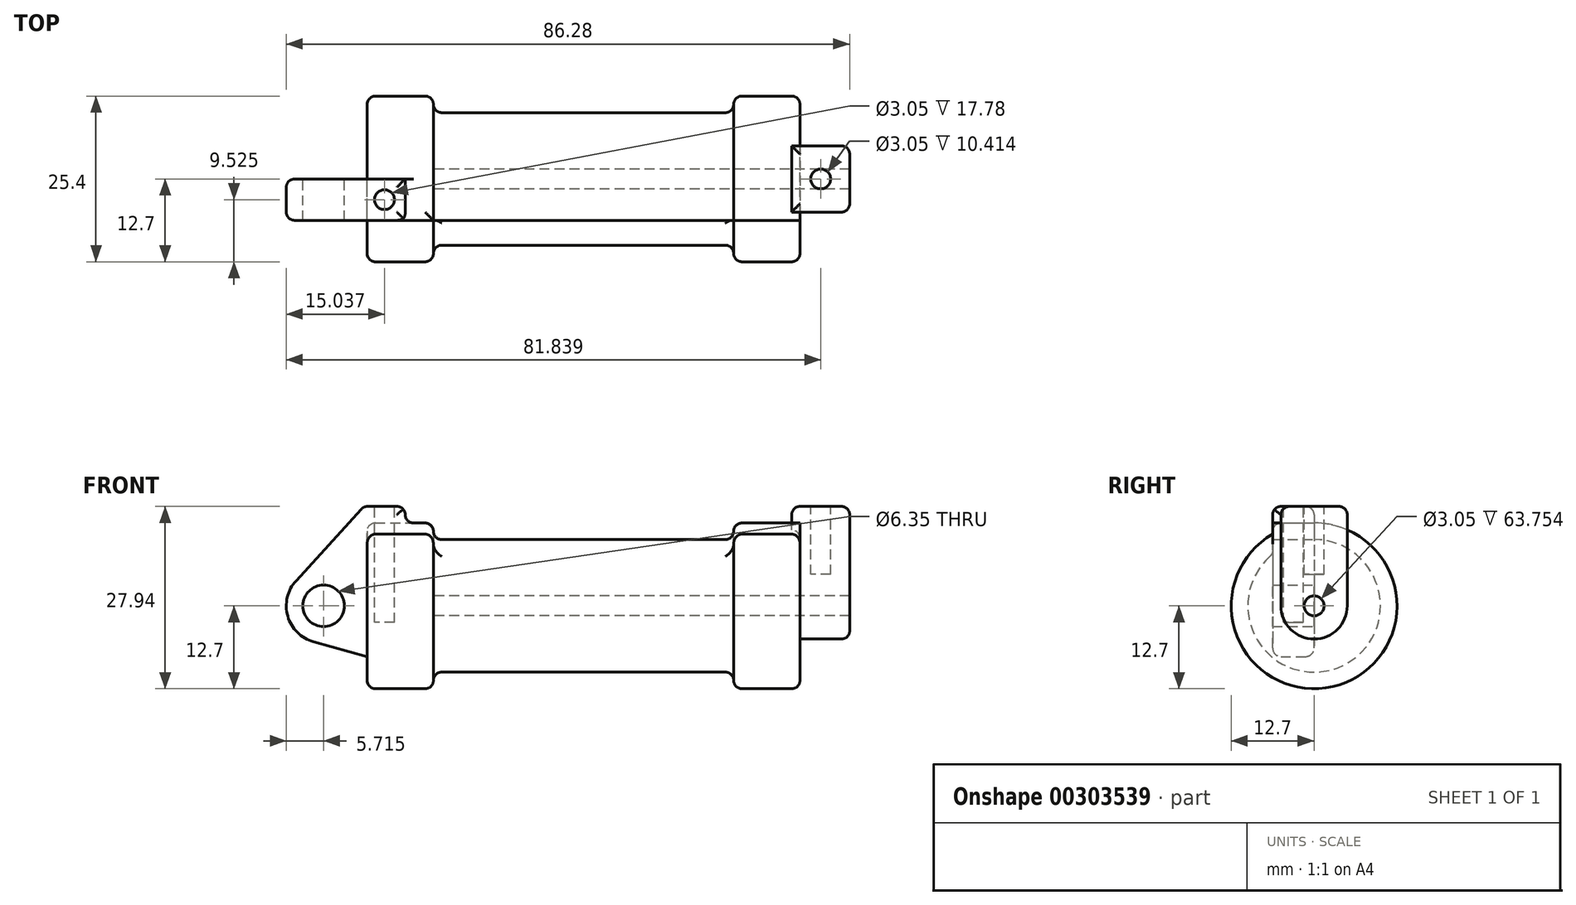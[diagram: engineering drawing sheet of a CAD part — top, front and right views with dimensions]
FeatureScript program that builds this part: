
annotation { "Feature Type Name" : "Feature", "Feature Type Description" : "" }
export const myFeature = defineFeature(function(context is Context, id is Id, definition is map)
    precondition{}
    {
        {
            var Q0;
            Q0=qCreatedBy(makeId("Front.planeOp"),FACE);
            var sketch = newSketch(context, id + "F0", { "sketchPlane" : qUnion([Q0])});
            skLineSegment(sketch, "E0", {"start": v(0, 0) * mm, "end": v(0, 12.7) * mm});
            skLineSegment(sketch, "E1", {"start": v(0, 12.7) * mm, "end": v(10.16, 12.7) * mm});
            skLineSegment(sketch, "E2", {"start": v(10.16, 12.7) * mm, "end": v(10.16, 10.16) * mm});
            skLineSegment(sketch, "E3", {"start": v(10.16, 10.16) * mm, "end": v(56.13, 10.16) * mm});
            skLineSegment(sketch, "E4", {"start": v(56.13, 10.16) * mm, "end": v(56.13, 12.7) * mm});
            skLineSegment(sketch, "E5", {"start": v(56.13, 12.7) * mm, "end": v(66.3, 12.7) * mm});
            skLineSegment(sketch, "E6", {"start": v(66.3, 12.7) * mm, "end": v(66.3, 0) * mm});
            skLineSegment(sketch, "E7", {"start": v(66.3, 0) * mm, "end": v(0, 0) * mm});
            skLineSegment(sketch, "E8", {"start": v(5.84, 15.24) * mm, "end": v(-0.5, 15.24) * mm});
            skLineSegment(sketch, "E9", {"start": v(-0.5, 15.24) * mm, "end": v(-10.88, 3.85) * mm});
            skLineSegment(sketch, "E10", {"start": v(0, 0) * mm, "end": v(-6.65, 0) * mm});
            skCircle(sketch, "E11", {"center": v(-6.65, 0) * mm, "radius": 5.72 * mm});
            skCircle(sketch, "E12", {"center": v(-6.65, 0) * mm, "radius": 3.18 * mm});
            skLineSegment(sketch, "E13", {"start": v(5.84, 15.24) * mm, "end": v(5.84, -9.4) * mm});
            skLineSegment(sketch, "E14", {"start": v(5.84, -9.4) * mm, "end": v(-8.18, -5.5) * mm});
            skSolve(sketch);
        }
        {
            var Q0;
            {var subQ0=sQuery(id+"F0.wireOp",EDGE,"E2");Q0=makeQuery(id+"F0.imprint","IMPRINT",FACE,{"disambiguationData":[TD([[makeQuery(id+"F0.imprint","IMPRINT",EDGE,{"derivedFrom":subQ0}),-1.0]])]});}
            var Q1;
            {var subQ0=sQuery(id+"F0.wireOp",EDGE,"E0");Q1=makeQuery(id+"F0.imprint","IMPRINT",FACE,{"disambiguationData":[TD([[makeQuery(id+"F0.imprint","IMPRINT",EDGE,{"derivedFrom":subQ0}),-1.0]])]});}
            var Q2;
            Q2=sQuery(id+"F0.wireOp",EDGE,"E7");
            revolve(context, id + "F1", {"entities" : qUnion([Q0, Q1]), "axis" : qUnion([Q2]), "revolveType" : RevolveType.FULL});
        }
        {
            var Q0;
            Q0 = qSketchRegion(id + "F0", true);
            extrude(context, id + "F2", {"entities" : qUnion([Q0]), "operationType" : NewBodyOperationType.ADD, "depth" : 6.35 * mm});
        }
        {
            var Q0;
            Q0=sQuery(id+"F0.wireOp",VERTEX,"E10.end");
            var Q1;
            Q1=makeQuery(id+"F1.opRevolve","SWEPT_BODY",BODY,{"disambiguationData":[OSD([sQuery(id+"F0.wireOp",EDGE,"E0"),sQuery(id+"F0.wireOp",EDGE,"E1"),sQuery(id+"F0.wireOp",EDGE,"E2"),sQuery(id+"F0.wireOp",EDGE,"E3"),sQuery(id+"F0.wireOp",EDGE,"E4"),sQuery(id+"F0.wireOp",EDGE,"E5"),sQuery(id+"F0.wireOp",EDGE,"E6"),sQuery(id+"F0.wireOp",EDGE,"E7")])]});
            hole(context, id + "F3", {"style" : HoleStyle.SIMPLE, "endStyle" : HoleEndStyle.THROUGH, "oppositeDirection" : true, "holeDiameter" : 6.35 * mm, "tappedDepth" : 12.7 * mm, "tapClearance" : 3, "locations" : qUnion([Q0]), "scope" : qUnion([Q1])});
        }
        {
            var Q0;
            {var subQ0=sQuery(id+"F0.wireOp",EDGE,"E6");Q0=makeQuery(id+"F2.boolean.opBoolean","MERGE",FACE,{"derivedFrom":[makeQuery(id+"F1.opRevolve","SWEPT_FACE",FACE,{"disambiguationData":[OSD([subQ0])]}),makeQuery(id+"F2.opExtrude","SWEPT_FACE",FACE,{"disambiguationData":[OSD([subQ0])]})]});}
            var sketch = newSketch(context, id + "F4", { "sketchPlane" : qUnion([Q0])});
            skCircle(sketch, "E15", {"center": v(0, 0) * mm, "radius": 1.52 * mm});
            skCircle(sketch, "E16", {"center": v(0, 0) * mm, "radius": 5.08 * mm});
            skLineSegment(sketch, "E17", {"start": v(-5.08, 0) * mm, "end": v(-5.08, 15.24) * mm});
            skLineSegment(sketch, "E18", {"start": v(5.08, 0) * mm, "end": v(5.08, 15.24) * mm});
            skLineSegment(sketch, "E19", {"start": v(5.08, 15.24) * mm, "end": v(-5.08, 15.24) * mm});
            skSolve(sketch);
        }
        {
            var Q0;
            Q0 = qSketchRegion(id + "F4", true);
            extrude(context, id + "F5", {"entities" : qUnion([Q0]), "operationType" : NewBodyOperationType.ADD, "depth" : 7.62 * mm});
        }
        {
            var Q0;
            Q0 = qSketchRegion(id + "F4", true);
            extrude(context, id + "F6", {"entities" : qUnion([Q0]), "operationType" : NewBodyOperationType.ADD, "oppositeDirection" : true, "depth" : 1.27 * mm});
        }
        {
            var Q0;
            {var subQ0=sQuery(id+"F0.wireOp",EDGE,"E6");Q0=makeQuery(id+"F5.boolean.opBoolean","SPLIT",FACE,{"disambiguationData":[TD([makeQuery(id+"F5.opExtrude","SWEPT_FACE",FACE,{"disambiguationData":[OSD([sQuery(id+"F4.wireOp",EDGE,"E15")])]})])],"derivedFrom":makeQuery(id+"F2.boolean.opBoolean","MERGE",FACE,{"derivedFrom":[makeQuery(id+"F1.opRevolve","SWEPT_FACE",FACE,{"disambiguationData":[OSD([subQ0])]}),makeQuery(id+"F2.opExtrude","SWEPT_FACE",FACE,{"disambiguationData":[OSD([subQ0])]})]})});}
            var Q1;
            {var subQ0=sQuery(id+"F0.wireOp",EDGE,"E2");Q1=makeQuery(id+"F2.boolean.opBoolean","MERGE",FACE,{"derivedFrom":[makeQuery(id+"F1.opRevolve","SWEPT_FACE",FACE,{"disambiguationData":[OSD([subQ0])]}),makeQuery(id+"F2.opExtrude","SWEPT_FACE",FACE,{"disambiguationData":[OSD([subQ0])]})]});}
            extrude(context, id + "F7", {"entities" : qUnion([Q0]), "operationType" : NewBodyOperationType.REMOVE, "endBound" : BoundingType.UP_TO_SURFACE, "oppositeDirection" : true, "endBoundEntityFace" : qUnion([Q1]), "depth" : 25.4 * mm});
        }
        {
            var Q0;
            Q0=makeQuery(id+"F2.opExtrude","SWEPT_FACE",FACE,{"disambiguationData":[OSD([sQuery(id+"F0.wireOp",EDGE,"E8")])]});
            var sketch = newSketch(context, id + "F8", { "sketchPlane" : qUnion([Q0])});
            skCircle(sketch, "E20", {"center": v(2.67, -3.18) * mm, "radius": 1.52 * mm});
            skPoint(sketch, "E20.centerSnap0", {"position": v(2.67, 0) * mm});
            skPoint(sketch, "E20.centerSnap1", {"position": v(5.84, -3.18) * mm});
            skSolve(sketch);
        }
        {
            var Q0;
            {var subQ0=sQuery(id+"F4.wireOp",EDGE,"E19");Q0=makeQuery(id+"F6.boolean.opBoolean","MERGE",FACE,{"derivedFrom":[makeQuery(id+"F5.opExtrude","SWEPT_FACE",FACE,{"disambiguationData":[OSD([subQ0])]}),makeQuery(id+"F6.opExtrude","SWEPT_FACE",FACE,{"disambiguationData":[OSD([subQ0])]})]});}
            var sketch = newSketch(context, id + "F9", { "sketchPlane" : qUnion([Q0])});
            skCircle(sketch, "E21", {"center": v(69.47, 0) * mm, "radius": 1.52 * mm});
            skPoint(sketch, "E21.centerSnap0", {"position": v(73.91, 0) * mm});
            skPoint(sketch, "E21.centerSnap1", {"position": v(69.47, 5.08) * mm});
            skSolve(sketch);
        }
        {
            var Q0;
            Q0=makeQuery(id+"F8.imprint","IMPRINT",FACE,{"disambiguationData":[TD([[makeQuery(id+"F8.imprint","IMPRINT",EDGE,{"derivedFrom":sQuery(id+"F8.wireOp",EDGE,"E20")}),1.0]])]});
            extrude(context, id + "F10", {"entities" : qUnion([Q0]), "operationType" : NewBodyOperationType.REMOVE, "oppositeDirection" : true, "depth" : 17.78 * mm});
        }
        {
            var Q0;
            Q0=makeQuery(id+"F9.imprint","IMPRINT",FACE,{"disambiguationData":[TD([[makeQuery(id+"F9.imprint","IMPRINT",EDGE,{"derivedFrom":sQuery(id+"F9.wireOp",EDGE,"E21")}),1.0]])]});
            extrude(context, id + "F11", {"entities" : qUnion([Q0]), "operationType" : NewBodyOperationType.REMOVE, "oppositeDirection" : true, "depth" : 10.4 * mm});
        }
        {
            var Q0;
            Q0=makeQuery(id+"F1.opRevolve","SWEPT_FACE",FACE,{"disambiguationData":[OSD([sQuery(id+"F0.wireOp",EDGE,"E3")])]});
            fillet(context, id + "F12", {"entities" : qUnion([Q0]), "radius" : 1.27 * mm, "tangentPropagation" : true, "allowEdgeOverflow" : false});
        }
        {
            var Q0;
            {var subQ0=sQuery(id+"F0.wireOp",EDGE,"E2");Q0=makeQuery(id+"F12.opFillet","BLEND_EDGE",EDGE,{"blendedFrom":[makeQuery(id+"F2.opExtrude","SWEPT_EDGE",EDGE,{"disambiguationData":[OSD([subQ0,sQuery(id+"F0.wireOp",EDGE,"E3")])]}),makeQuery(id+"F2.boolean.opBoolean","MERGE",FACE,{"derivedFrom":[makeQuery(id+"F1.opRevolve","SWEPT_FACE",FACE,{"disambiguationData":[OSD([subQ0])]}),makeQuery(id+"F2.opExtrude","SWEPT_FACE",FACE,{"disambiguationData":[OSD([subQ0])]})]})],"blendedInto":[makeQuery(id+"F2.boolean.opBoolean","MERGE",FACE,{"derivedFrom":[makeQuery(id+"F1.opRevolve","SWEPT_FACE",FACE,{"disambiguationData":[OSD([subQ0])]}),makeQuery(id+"F2.opExtrude","SWEPT_FACE",FACE,{"disambiguationData":[OSD([subQ0])]})]})]});}
            var Q1;
            {var subQ0=sQuery(id+"F0.wireOp",EDGE,"E2");Q1=makeQuery(id+"F12.opFillet","BLEND_EDGE",EDGE,{"blendedFrom":[makeQuery(id+"F1.opRevolve","SWEPT_EDGE",EDGE,{"disambiguationData":[OSD([subQ0,sQuery(id+"F0.wireOp",EDGE,"E3")])]}),makeQuery(id+"F2.boolean.opBoolean","MERGE",FACE,{"derivedFrom":[makeQuery(id+"F1.opRevolve","SWEPT_FACE",FACE,{"disambiguationData":[OSD([subQ0])]}),makeQuery(id+"F2.opExtrude","SWEPT_FACE",FACE,{"disambiguationData":[OSD([subQ0])]})]})],"blendedInto":[makeQuery(id+"F2.boolean.opBoolean","MERGE",FACE,{"derivedFrom":[makeQuery(id+"F1.opRevolve","SWEPT_FACE",FACE,{"disambiguationData":[OSD([subQ0])]}),makeQuery(id+"F2.opExtrude","SWEPT_FACE",FACE,{"disambiguationData":[OSD([subQ0])]})]})]});}
            var Q2;
            Q2=makeQuery(id+"F2.opExtrude","SWEPT_FACE",FACE,{"disambiguationData":[OSD([sQuery(id+"F0.wireOp",EDGE,"E1")])]});
            var Q3;
            Q3=makeQuery(id+"F2.opExtrude","SWEPT_EDGE",EDGE,{"disambiguationData":[OSD([sQuery(id+"F0.wireOp",EDGE,"E8"),sQuery(id+"F0.wireOp",EDGE,"E13")])]});
            var Q4;
            Q4=makeQuery(id+"F2.opExtrude","CAP_EDGE",EDGE,{"disambiguationData":[OSD([sQuery(id+"F0.wireOp",EDGE,"E8")])],"isStart":false});
            var Q5;
            Q5=makeQuery(id+"F2.opExtrude","SWEPT_EDGE",EDGE,{"disambiguationData":[OSD([sQuery(id+"F0.wireOp",EDGE,"E8"),sQuery(id+"F0.wireOp",EDGE,"E9")])]});
            var Q6;
            Q6=makeQuery(id+"F2.opExtrude","CAP_EDGE",EDGE,{"disambiguationData":[OSD([sQuery(id+"F0.wireOp",EDGE,"E8")])],"isStart":true});
            var Q7;
            Q7=makeQuery(id+"F2.opExtrude","SWEPT_FACE",FACE,{"disambiguationData":[OSD([sQuery(id+"F0.wireOp",EDGE,"E9")])]});
            var Q8;
            Q8=makeQuery(id+"F2.opExtrude","CAP_EDGE",EDGE,{"disambiguationData":[OSD([sQuery(id+"F0.wireOp",EDGE,"E14")])],"isStart":false});
            var Q9;
            Q9=makeQuery(id+"F2.opExtrude","CAP_EDGE",EDGE,{"disambiguationData":[OSD([sQuery(id+"F0.wireOp",EDGE,"E11")])],"isStart":false});
            var Q10;
            Q10=makeQuery(id+"F2.opExtrude","SWEPT_FACE",FACE,{"disambiguationData":[OSD([sQuery(id+"F0.wireOp",EDGE,"E11")])]});
            var Q11;
            Q11=makeQuery(id+"F2.opExtrude","CAP_EDGE",EDGE,{"disambiguationData":[OSD([sQuery(id+"F0.wireOp",EDGE,"E9")])],"isStart":false});
            var Q12;
            Q12=makeQuery(id+"F1.opRevolve","SWEPT_EDGE",EDGE,{"disambiguationData":[OSD([sQuery(id+"F0.wireOp",EDGE,"E0"),sQuery(id+"F0.wireOp",EDGE,"E1")])]});
            fillet(context, id + "F13", {"entities" : qUnion([Q0, Q1, Q2, Q3, Q4, Q5, Q6, Q7, Q8, Q9, Q10, Q11, Q12]), "radius" : 1.27 * mm, "tangentPropagation" : true, "allowEdgeOverflow" : false});
        }
        {
            var Q0;
            {var subQ0=sQuery(id+"F0.wireOp",EDGE,"E5");var subQ1=sQuery(id+"F0.wireOp",EDGE,"E6");Q0=makeQuery(id+"F5.boolean.opBoolean","SPLIT",EDGE,{"disambiguationData":[topologyDisambiguationEdgeConnected([makeQuery(id+"F1.opRevolve","SWEPT_FACE",FACE,{"disambiguationData":[OSD([subQ1])]})])],"derivedFrom":makeQuery(id+"F1.opRevolve","SWEPT_EDGE",EDGE,{"disambiguationData":[OSD([subQ0,subQ1])]})});}
            var Q1;
            Q1=makeQuery(id+"F1.opRevolve","SWEPT_EDGE",EDGE,{"disambiguationData":[OSD([sQuery(id+"F0.wireOp",EDGE,"E4"),sQuery(id+"F0.wireOp",EDGE,"E5")])]});
            var Q2;
            {var subQ0=sQuery(id+"F4.wireOp",EDGE,"E19");var subQ1=sQuery(id+"F4.wireOp",EDGE,"E17");Q2=makeQuery(id+"F6.boolean.opBoolean","MERGE",EDGE,{"derivedFrom":[makeQuery(id+"F5.opExtrude","SWEPT_EDGE",EDGE,{"disambiguationData":[OSD([subQ1,subQ0])]}),makeQuery(id+"F6.opExtrude","SWEPT_EDGE",EDGE,{"disambiguationData":[OSD([subQ1,subQ0])]})]});}
            var Q3;
            Q3=makeQuery(id+"F6.opExtrude","CAP_EDGE",EDGE,{"disambiguationData":[OSD([sQuery(id+"F4.wireOp",EDGE,"E19")])],"isStart":false});
            var Q4;
            {var subQ0=sQuery(id+"F4.wireOp",EDGE,"E19");var subQ1=sQuery(id+"F4.wireOp",EDGE,"E18");Q4=makeQuery(id+"F6.boolean.opBoolean","MERGE",EDGE,{"derivedFrom":[makeQuery(id+"F5.opExtrude","SWEPT_EDGE",EDGE,{"disambiguationData":[OSD([subQ1,subQ0])]}),makeQuery(id+"F6.opExtrude","SWEPT_EDGE",EDGE,{"disambiguationData":[OSD([subQ1,subQ0])]})]});}
            var Q5;
            Q5=makeQuery(id+"F5.opExtrude","CAP_EDGE",EDGE,{"disambiguationData":[OSD([sQuery(id+"F4.wireOp",EDGE,"E19")])],"isStart":false});
            var Q6;
            Q6=makeQuery(id+"F5.opExtrude","CAP_EDGE",EDGE,{"disambiguationData":[OSD([sQuery(id+"F4.wireOp",EDGE,"E17")])],"isStart":false});
            var Q7;
            Q7=makeQuery(id+"F5.opExtrude","CAP_EDGE",EDGE,{"disambiguationData":[OSD([sQuery(id+"F4.wireOp",EDGE,"E16")])],"isStart":false});
            var Q8;
            Q8=makeQuery(id+"F5.opExtrude","CAP_EDGE",EDGE,{"disambiguationData":[OSD([sQuery(id+"F4.wireOp",EDGE,"E18")])],"isStart":false});
            var Q9;
            Q9=makeQuery(id+"F5.opExtrude","SWEPT_EDGE",EDGE,{"disambiguationData":[OSD([sQuery(id+"F4.wireOp",EDGE,"E16"),sQuery(id+"F4.wireOp",EDGE,"E17")])]});
            var Q10;
            Q10=makeQuery(id+"F5.opExtrude","SWEPT_EDGE",EDGE,{"disambiguationData":[OSD([sQuery(id+"F4.wireOp",EDGE,"E16"),sQuery(id+"F4.wireOp",EDGE,"E18")])]});
            fillet(context, id + "F14", {"entities" : qUnion([Q0, Q1, Q2, Q3, Q4, Q5, Q6, Q7, Q8, Q9, Q10]), "radius" : 1.27 * mm, "tangentPropagation" : true, "allowEdgeOverflow" : false});
        }
    });
